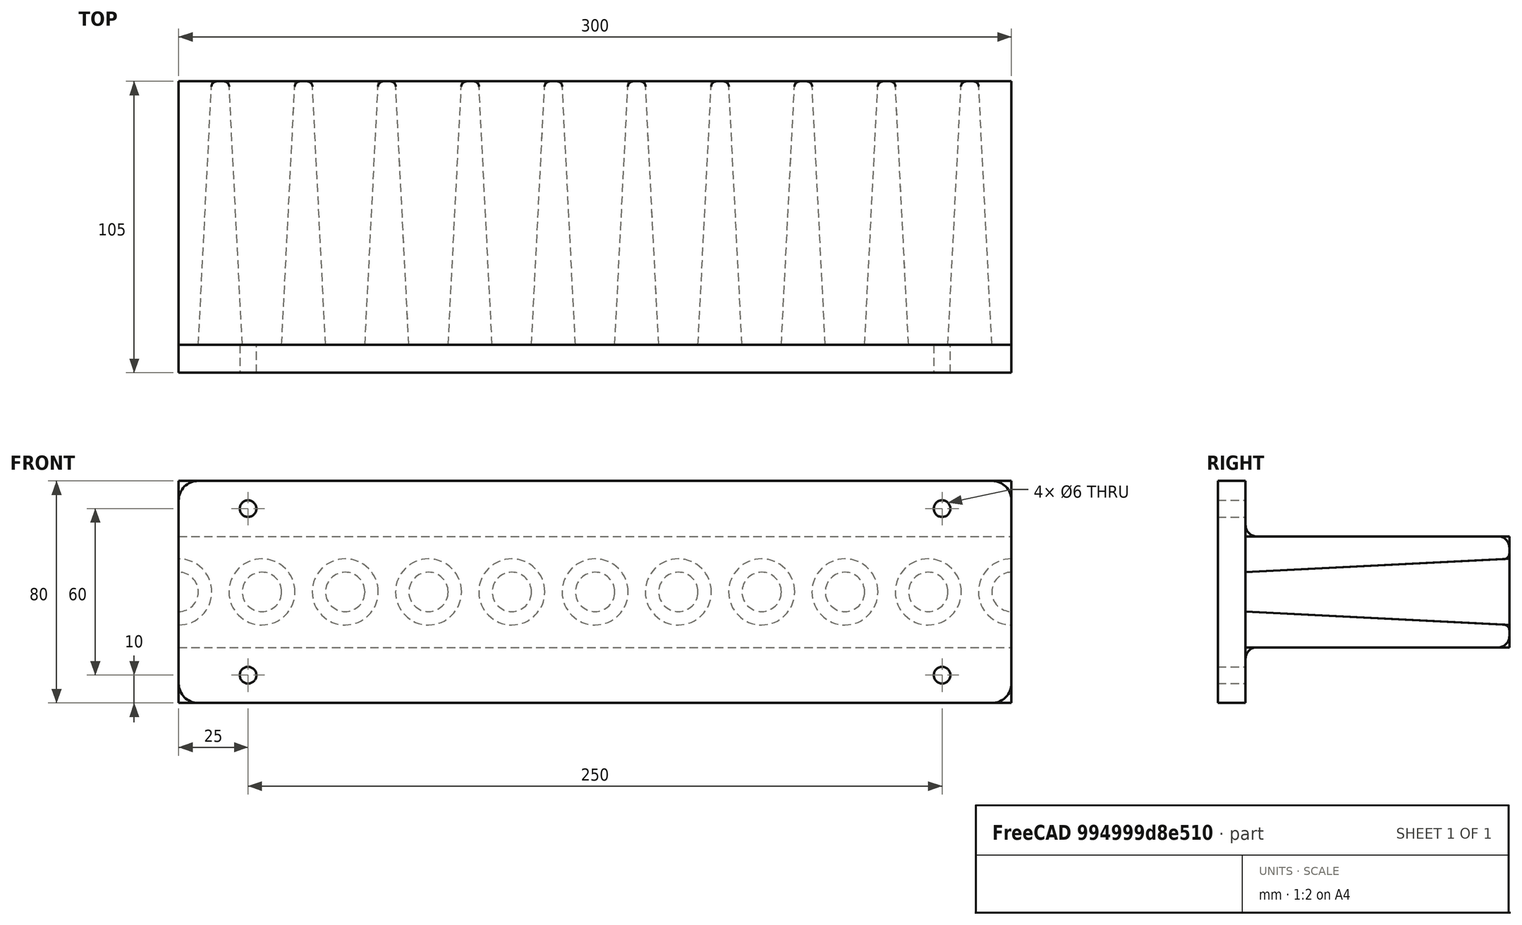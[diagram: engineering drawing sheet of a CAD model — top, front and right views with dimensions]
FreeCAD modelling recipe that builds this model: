
FCSTD DOCUMENT  (FreeCAD 0.16R)
Label: MT3holde2
License: All rights reserved
LicenseURL: http://en.wikipedia.org/wiki/All_rights_reserved
objects: Sketcher::SketchObject×4, PartDesign::Fillet×4, PartDesign::Pad×2, PartDesign::Groove×1, PartDesign::LinearPattern×1, PartDesign::Pocket×1, Mesh::Feature×1
note: 17 computed .brp shape members not serialized (recipe doc carries the construction recipe); baked Part::Feature solids carry a one-line shape summary decoded from their .brp

FEATURE [Sketcher::SketchObject] Sketch002
  sketch-geometry (4):
    g0: LineSegment StartX=-150 StartY=0 StartZ=0 EndX=150 EndY=0 EndZ=0
    g1: LineSegment StartX=150 StartY=0 StartZ=0 EndX=150 EndY=-95 EndZ=0
    g2: LineSegment StartX=150 StartY=-95 StartZ=0 EndX=-150 EndY=-95 EndZ=0
    g3: LineSegment StartX=-150 StartY=-95 StartZ=0 EndX=-150 EndY=0 EndZ=0
  constraints (12):
    c: Coincident(g0,g1)
    c: Coincident(g1,g2)
    c: Coincident(g2,g3)
    c: Coincident(g3,g0)
    c: Horizontal(g0)
    c: Horizontal(g2)
    c: Vertical(g1)
    c: Vertical(g3)
    c: PointOnObject(g0,g-1)
    c: Symmetric(g0,g0,g-2)
    c: Distance(g2) = 300
    c: Distance(g1) = 95
FEATURE [PartDesign::Pad] Pad
  Length = 40
  Length2 = 100
  Midplane = true
  Sketch = -> Sketch002
  Type = 0
FEATURE [Sketcher::SketchObject] Sketch
  Placement = pos=(-150,0,0) rot=(0.57735,-0.57735,-0.57735;2.0944rad)
  Support = -> Pad [Face4]
  sketch-geometry (4):
    g0: LineSegment StartX=0 StartY=-11.9 StartZ=0 EndX=0 EndY=0 EndZ=0
    g1: LineSegment StartX=0 StartY=0 StartZ=0 EndX=95 EndY=0 EndZ=0
    g2: LineSegment StartX=0 StartY=-11.9 StartZ=0 EndX=95 EndY=-7.08751 EndZ=0
    g3: LineSegment StartX=95 StartY=-7.08751 StartZ=0 EndX=95 EndY=0 EndZ=0
  constraints (11):
    c: PointOnObject(g0,g-2)
    c: Coincident(g0,g-1)
    c: Coincident(g0,g1)
    c: PointOnObject(g1,g-1)
    c: Coincident(g0,g2)
    c: Distance(g0) = 11.9
    c: Angle(g2) = 0.0506145
    c: Coincident(g3,g2)
    c: Vertical(g3)
    c: Coincident(g3,g1)
    c: Distance(g1) = 95
FEATURE [PartDesign::Groove] Groove
  Angle = 360
  Axis = (0,-1,0)
  Base = (-150,0,0)
  ReferenceAxis = -> Sketch [H_Axis]
  Sketch = -> Sketch
FEATURE [PartDesign::LinearPattern] LinearPattern
  Direction = -> Groove [Face3]
  Length = 300
  Occurrences = 11
  Originals = -> [Groove]
FEATURE [Sketcher::SketchObject] Sketch003
  ExternalGeometry = -> [LinearPattern]
  Placement = pos=(0,-95,0) rot=(1,0,0;1.5708rad)
  Support = -> LinearPattern [Face19]
  sketch-geometry (4):
    g0: LineSegment StartX=-150 StartY=40 StartZ=0 EndX=150 EndY=40 EndZ=0
    g1: LineSegment StartX=150 StartY=40 StartZ=0 EndX=150 EndY=-40 EndZ=0
    g2: LineSegment StartX=150 StartY=-40 StartZ=0 EndX=-150 EndY=-40 EndZ=0
    g3: LineSegment StartX=-150 StartY=-40 StartZ=0 EndX=-150 EndY=40 EndZ=0
  constraints (12):
    c: Coincident(g0,g1)
    c: Coincident(g1,g2)
    c: Coincident(g2,g3)
    c: Coincident(g3,g0)
    c: Horizontal(g0)
    c: Horizontal(g2)
    c: Vertical(g1)
    c: Vertical(g3)
    c: PointOnObject(g-4,g3)
    c: PointOnObject(g-4,g1)
    c: Symmetric(g0,g2,g-1)
    c: Distance(g3) = 80
FEATURE [PartDesign::Pad] Pad001
  Length = 10
  Length2 = 100
  Sketch = -> Sketch003
  Type = 0
FEATURE [Sketcher::SketchObject] Sketch004
  ExternalGeometry = -> [Pad001]
  Placement = pos=(0,-95,0) rot=(0,0.707107,0.707107;3.14159rad)
  Support = -> Pad001 [Face7]
  sketch-geometry (6):
    g0: Circle CenterX=-125 CenterY=30 CenterZ=0 NormalX=0 NormalY=0 NormalZ=1 Radius=3
    g1: Circle CenterX=125 CenterY=30 CenterZ=0 NormalX=0 NormalY=0 NormalZ=1 Radius=3
    g2: Circle CenterX=125 CenterY=-30 CenterZ=0 NormalX=0 NormalY=0 NormalZ=1 Radius=3
    g3: Circle CenterX=-125 CenterY=-30 CenterZ=0 NormalX=0 NormalY=0 NormalZ=1 Radius=3
    g4: LineSegment [constr] StartX=-125 StartY=71.6389 StartZ=0 EndX=-125 EndY=-73.3668 EndZ=0
    g5: LineSegment [constr] StartX=125 StartY=68.858 StartZ=0 EndX=125 EndY=-67.8049 EndZ=0
  constraints (16):
    c: Radius(g0) = 3
    c: Equal(g0,g1)
    c: Equal(g0,g2)
    c: Equal(g0,g3)
    c: Vertical(g4)
    c: Vertical(g5)
    c: Distance(g-5,g5) = 25
    c: Distance(g-3,g4) = 25
    c: PointOnObject(g0,g4)
    c: PointOnObject(g3,g4)
    c: PointOnObject(g1,g5)
    c: PointOnObject(g2,g5)
    c: Distance(g3,g-6) = 10
    c: Distance(g0,g-10) = 10
    c: Distance(g1,g-10) = 10
    c: Distance(g2,g-6) = 10
FEATURE [PartDesign::Pocket] Pocket
  Length = 5
  Sketch = -> Sketch004
  Type = 1
FEATURE [PartDesign::Fillet] Fillet
  Base = -> Pocket [Edge1,Edge5,Edge15,Edge2]
  Radius = 7
FEATURE [Mesh::Feature] Mesh  label="Fillet (Meshed)"
FEATURE [PartDesign::Fillet] Fillet001
  Base = -> Fillet [Edge49,Edge7]
  Radius = 4
FEATURE [PartDesign::Fillet] Fillet002
  Base = -> Fillet001 [Edge62,Edge72]
  Radius = 4
FEATURE [PartDesign::Fillet] Fillet003
  Base = -> Fillet002 [Edge27,Edge18,Edge16,Edge21,Edge22,Edge23,Edge26,Edge25,Edge24,Edge29,Edge28]
  Radius = 2
